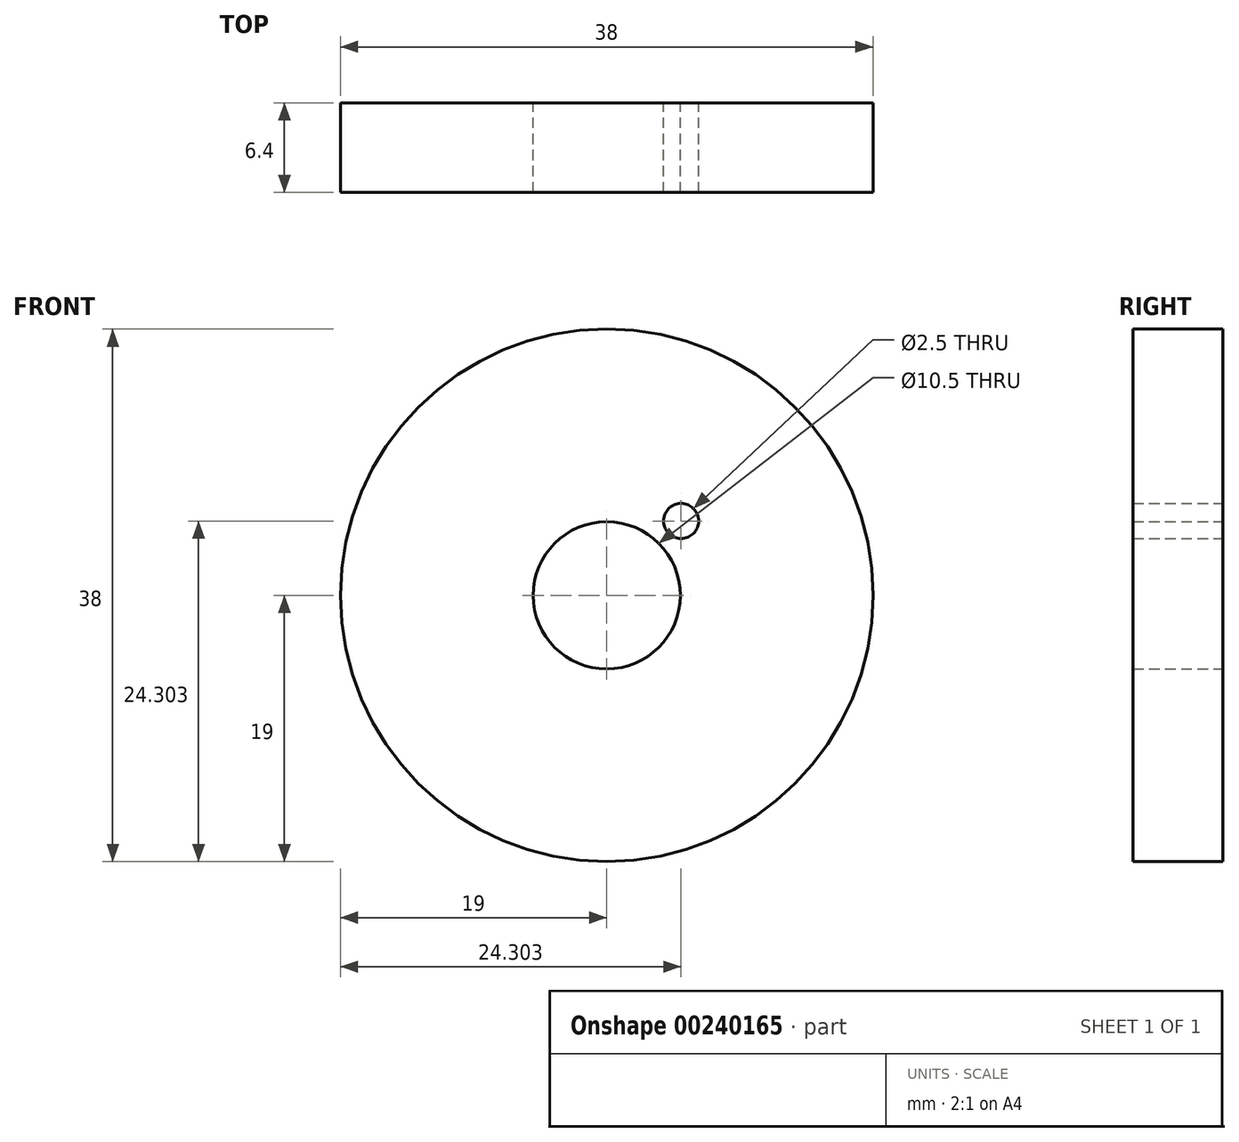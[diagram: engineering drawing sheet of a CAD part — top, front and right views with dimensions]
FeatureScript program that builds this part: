
annotation { "Feature Type Name" : "Feature", "Feature Type Description" : "" }
export const myFeature = defineFeature(function(context is Context, id is Id, definition is map)
    precondition{}
    {
        {
            var Q0;
            Q0=qCreatedBy(makeId("Front.planeOp"),FACE);
            var sketch = newSketch(context, id + "F0", { "sketchPlane" : qUnion([Q0])});
            skCircle(sketch, "E0", {"center": v(0, 0) * mm, "radius": 19 * mm});
            skSolve(sketch);
        }
        {
            var Q0;
            Q0=makeQuery(id+"F0.imprint","IMPRINT",FACE,{"disambiguationData":[TD([[makeQuery(id+"F0.imprint","IMPRINT",EDGE,{"derivedFrom":sQuery(id+"F0.wireOp",EDGE,"E0")}),1.0]])]});
            extrude(context, id + "F1", {"entities" : qUnion([Q0]), "depth" : 6.4 * mm});
        }
        {
            var Q0;
            Q0=qCreatedBy(makeId("Front.planeOp"),FACE);
            var sketch = newSketch(context, id + "F2", { "sketchPlane" : qUnion([Q0])});
            skLineSegment(sketch, "E1", {"start": v(0, 0) * mm, "end": v(18.26, 18.26) * mm, "construction": true});
            skCircle(sketch, "E2", {"center": v(0, 0) * mm, "radius": 7.5 * mm, "construction": true});
            skCircle(sketch, "E3", {"center": v(5.3, 5.3) * mm, "radius": 1.25 * mm});
            skSolve(sketch);
        }
        {
            var Q0;
            Q0 = qSketchRegion(id + "F2", true);
            extrude(context, id + "F3", {"entities" : qUnion([Q0]), "operationType" : NewBodyOperationType.REMOVE, "depth" : 25.4 * mm});
        }
        {
            var Q0;
            Q0=qCreatedBy(makeId("Front.planeOp"),FACE);
            var sketch = newSketch(context, id + "F4", { "sketchPlane" : qUnion([Q0])});
            skCircle(sketch, "E4", {"center": v(0, 0) * mm, "radius": 5.25 * mm});
            skSolve(sketch);
        }
        {
            var Q0;
            Q0 = qSketchRegion(id + "F4", true);
            extrude(context, id + "F5", {"entities" : qUnion([Q0]), "operationType" : NewBodyOperationType.REMOVE, "endBound" : BoundingType.THROUGH_ALL, "depth" : 25.4 * mm});
        }
    });
